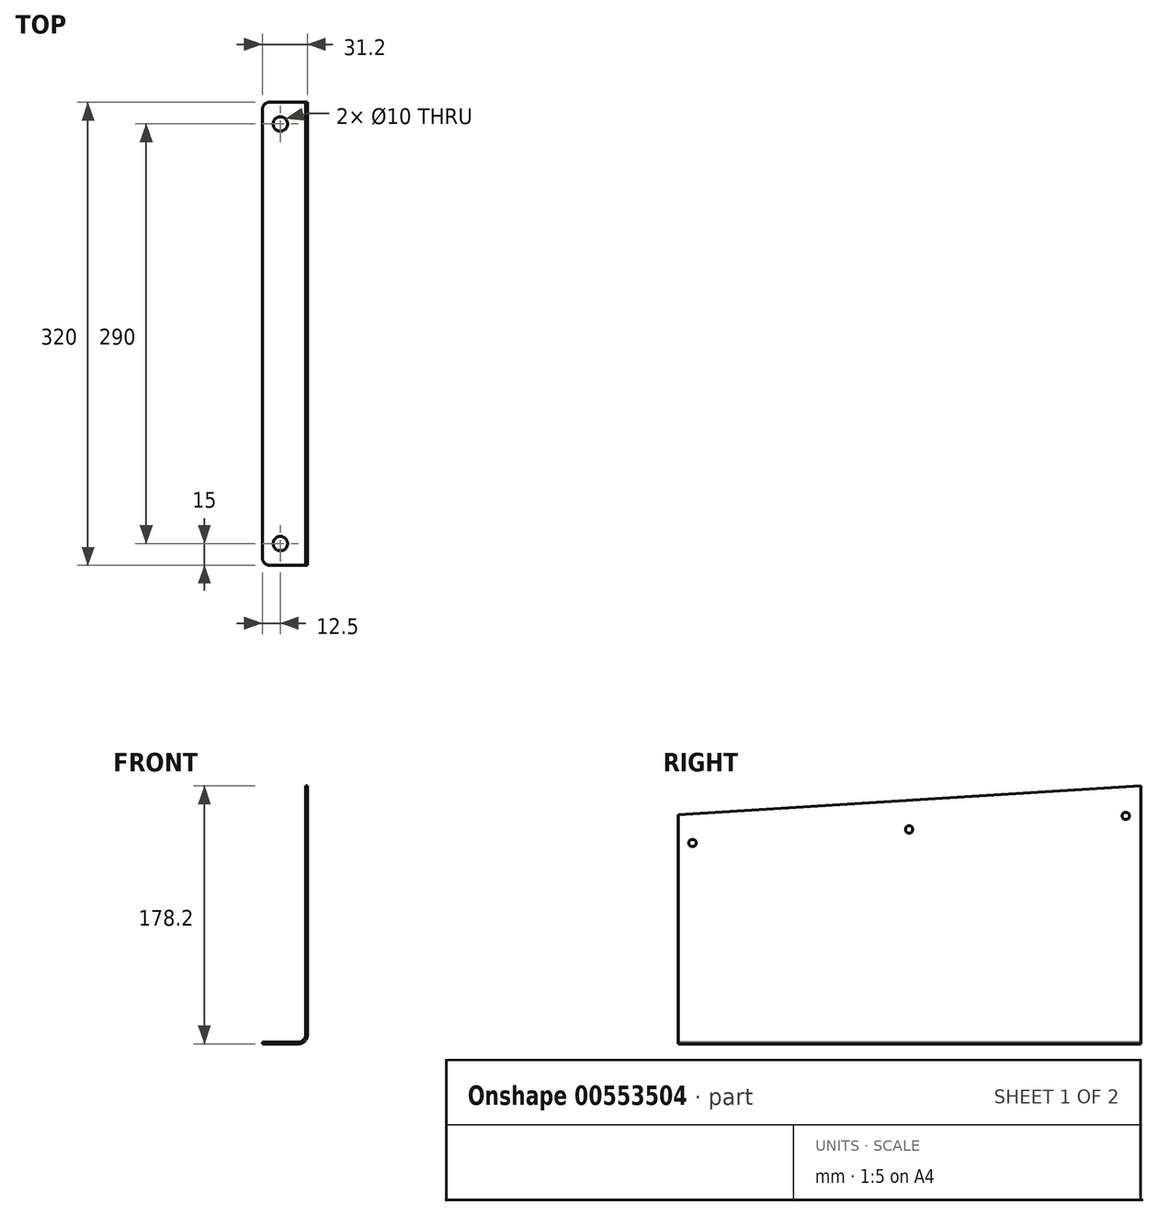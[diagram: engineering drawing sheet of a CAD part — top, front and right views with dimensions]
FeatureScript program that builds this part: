
annotation { "Feature Type Name" : "Feature", "Feature Type Description" : "" }
export const myFeature = defineFeature(function(context is Context, id is Id, definition is map)
    precondition{}
    {
        {
            var Q0;
            Q0=qCreatedBy(makeId("Front.planeOp"),FACE);
            var sketch = newSketch(context, id + "F0", { "sketchPlane" : qUnion([Q0])});
            skLineSegment(sketch, "E0", {"start": v(0, 0) * mm, "end": v(0, -207) * mm});
            skLineSegment(sketch, "E1", {"start": v(-5, -212) * mm, "end": v(-30, -212) * mm});
            skLineSegment(sketch, "E2", {"start": v(-30, -212) * mm, "end": v(-30, -213.2) * mm});
            skLineSegment(sketch, "E3", {"start": v(-30, -213.2) * mm, "end": v(-5, -213.2) * mm});
            skLineSegment(sketch, "E4", {"start": v(1.2, -207) * mm, "end": v(1.2, 0) * mm});
            skLineSegment(sketch, "E5", {"start": v(1.2, 0) * mm, "end": v(0, 0) * mm});
            skPoint(sketch, "E6.visualSharp", {"position": v(0, -212) * mm});
            skArc(sketch, "E6.filletArc", {"start": v(-5, -212) * mm, "mid": v(-1.46, -210.54) * mm, "end": v(0, -207) * mm});
            skPoint(sketch, "E7.visualSharp", {"position": v(1.2, -213.2) * mm});
            skArc(sketch, "E7.filletArc", {"start": v(-5, -213.2) * mm, "mid": v(-0.62, -211.38) * mm, "end": v(1.2, -207) * mm});
            skSolve(sketch);
        }
        {
            var Q0;
            Q0 = qSketchRegion(id + "F0", true);
            extrude(context, id + "F1", {"entities" : qUnion([Q0]), "oppositeDirection" : true, "depth" : 320 * mm, "offsetDistance" : 25 * mm});
        }
        {
            var Q0;
            Q0=makeQuery(id+"F1.opExtrude","SWEPT_FACE",FACE,{"disambiguationData":[OSD([sQuery(id+"F0.wireOp",EDGE,"E1")])]});
            var sketch = newSketch(context, id + "F2", { "sketchPlane" : qUnion([Q0])});
            skCircle(sketch, "E8", {"center": v(-17.5, 305) * mm, "radius": 5 * mm});
            skCircle(sketch, "E9.0.1.0", {"center": v(-17.5, 15) * mm, "radius": 5 * mm});
            skLineSegment(sketch, "E9.direction1", {"start": v(-17.5, 305) * mm, "end": v(7.5, 305) * mm, "construction": true});
            skLineSegment(sketch, "E9.direction2", {"start": v(-17.5, 305) * mm, "end": v(-17.5, 15) * mm, "construction": true});
            skSolve(sketch);
        }
        {
            var Q0;
            Q0 = qSketchRegion(id + "F2", true);
            extrude(context, id + "F3", {"entities" : qUnion([Q0]), "operationType" : NewBodyOperationType.REMOVE, "endBound" : BoundingType.UP_TO_NEXT, "oppositeDirection" : true, "depth" : 25 * mm, "offsetDistance" : 25 * mm});
        }
        {
            var Q0;
            Q0=makeQuery(id+"F1.opExtrude","CAP_EDGE",EDGE,{"disambiguationData":[OSD([sQuery(id+"F0.wireOp",EDGE,"E2")])],"isStart":false});
            var Q1;
            Q1=makeQuery(id+"F1.opExtrude","CAP_EDGE",EDGE,{"disambiguationData":[OSD([sQuery(id+"F0.wireOp",EDGE,"E2")])],"isStart":true});
            fillet(context, id + "F4", {"entities" : qUnion([Q0, Q1]), "radius" : 5 * mm, "tangentPropagation" : true, "allowEdgeOverflow" : false});
        }
        {
            var Q0;
            Q0=makeQuery(id+"F1.opExtrude","SWEPT_FACE",FACE,{"disambiguationData":[OSD([sQuery(id+"F0.wireOp",EDGE,"E0")])]});
            var sketch = newSketch(context, id + "F5", { "sketchPlane" : qUnion([Q0])});
            skLineSegment(sketch, "E10.0", {"start": v(-320, 0) * mm, "end": v(0, 0) * mm});
            skLineSegment(sketch, "E11", {"start": v(0, 0) * mm, "end": v(0, -55) * mm});
            skLineSegment(sketch, "E12", {"start": v(0, -55) * mm, "end": v(-320, -35) * mm});
            skLineSegment(sketch, "E13", {"start": v(-320, 0) * mm, "end": v(-320, -35) * mm});
            skSolve(sketch);
        }
        {
            var Q0;
            Q0 = qSketchRegion(id + "F5", true);
            extrude(context, id + "F6", {"entities" : qUnion([Q0]), "operationType" : NewBodyOperationType.REMOVE, "endBound" : BoundingType.UP_TO_NEXT, "oppositeDirection" : true, "depth" : 25 * mm, "offsetDistance" : 25 * mm});
        }
        {
            var Q0;
            Q0=makeQuery(id+"F1.opExtrude","SWEPT_FACE",FACE,{"disambiguationData":[OSD([sQuery(id+"F0.wireOp",EDGE,"E4")])]});
            var sketch = newSketch(context, id + "F7", { "sketchPlane" : qUnion([Q0])});
            skCircle(sketch, "E14", {"center": v(10, -74.41) * mm, "radius": 2.5 * mm});
            skCircle(sketch, "E15.1.0.0", {"center": v(159.7, -65.06) * mm, "radius": 2.5 * mm});
            skCircle(sketch, "E15.2.0.0", {"center": v(309.42, -55.7) * mm, "radius": 2.5 * mm});
            skLineSegment(sketch, "E15.direction1", {"start": v(10, -74.41) * mm, "end": v(159.7, -65.06) * mm, "construction": true});
            skSolve(sketch);
        }
        {
            var Q0;
            Q0 = qSketchRegion(id + "F7", true);
            extrude(context, id + "F8", {"entities" : qUnion([Q0]), "operationType" : NewBodyOperationType.REMOVE, "endBound" : BoundingType.UP_TO_NEXT, "oppositeDirection" : true, "depth" : 25 * mm, "offsetDistance" : 25 * mm});
        }
    });
